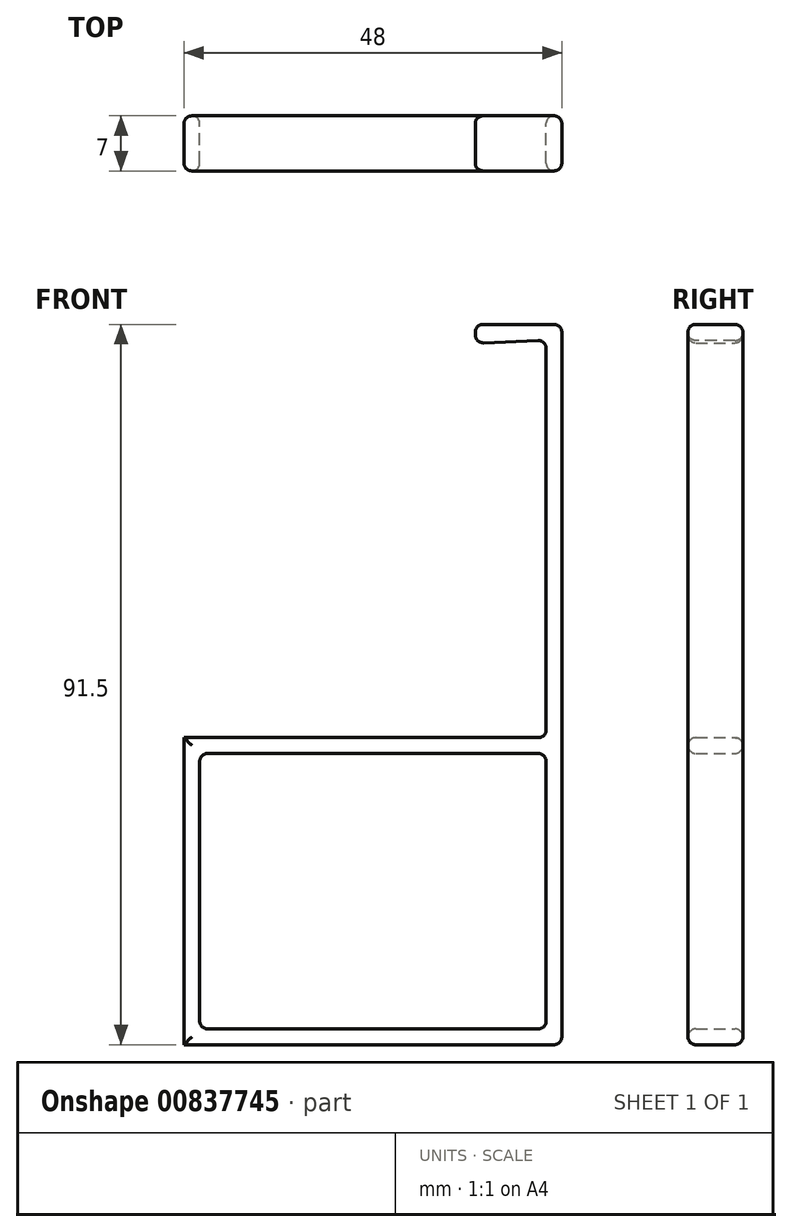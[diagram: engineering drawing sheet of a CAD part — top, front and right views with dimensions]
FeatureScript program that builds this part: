
annotation { "Feature Type Name" : "Feature", "Feature Type Description" : "" }
export const myFeature = defineFeature(function(context is Context, id is Id, definition is map)
    precondition{}
    {
        {
            var Q0;
            Q0=qCreatedBy(makeId("Front.planeOp"),FACE);
            var sketch = newSketch(context, id + "F0", { "sketchPlane" : qUnion([Q0])});
            skLineSegment(sketch, "E0", {"start": v(-54.27, 63.8) * mm, "end": v(-45.27, 64.18) * mm});
            skLineSegment(sketch, "E1", {"start": v(-45.27, 64.18) * mm, "end": v(-45.27, 13.68) * mm});
            skLineSegment(sketch, "E2", {"start": v(-45.27, 13.68) * mm, "end": v(-45.27, 13.68) * mm});
            skLineSegment(sketch, "E3", {"start": v(-45.27, -23.32) * mm, "end": v(-89.27, -23.32) * mm});
            skLineSegment(sketch, "E4", {"start": v(-91.27, -23.32) * mm, "end": v(-91.27, -25.32) * mm});
            skLineSegment(sketch, "E5", {"start": v(-91.27, -25.32) * mm, "end": v(-43.27, -25.32) * mm});
            skLineSegment(sketch, "E6", {"start": v(-43.27, -25.32) * mm, "end": v(-43.27, 66.18) * mm});
            skLineSegment(sketch, "E7", {"start": v(-43.27, 66.18) * mm, "end": v(-54.27, 66.18) * mm});
            skLineSegment(sketch, "E8", {"start": v(-54.27, 66.18) * mm, "end": v(-54.27, 63.8) * mm});
            skLineSegment(sketch, "E9", {"start": v(-45.27, 11.68) * mm, "end": v(-45.27, 11.68) * mm});
            skLineSegment(sketch, "E10", {"start": v(-45.27, 11.68) * mm, "end": v(-45.27, -23.32) * mm});
            skLineSegment(sketch, "E11", {"start": v(-45.27, 13.68) * mm, "end": v(-91.27, 13.68) * mm});
            skLineSegment(sketch, "E12", {"start": v(-91.27, 13.68) * mm, "end": v(-91.27, 11.68) * mm});
            skLineSegment(sketch, "E13", {"start": v(-89.27, 11.68) * mm, "end": v(-45.27, 11.68) * mm});
            skLineSegment(sketch, "E14", {"start": v(-91.27, 11.68) * mm, "end": v(-91.27, -23.32) * mm});
            skLineSegment(sketch, "E15", {"start": v(-89.27, -23.32) * mm, "end": v(-89.27, 11.68) * mm});
            skSolve(sketch);
        }
        {
            var Q0;
            Q0=makeQuery(id+"F0.imprint","IMPRINT",FACE,{"disambiguationData":[TD([[makeQuery(id+"F0.imprint","IMPRINT",EDGE,{"derivedFrom":sQuery(id+"F0.wireOp",EDGE,"E0")}),1.0]])]});
            extrude(context, id + "F1", {"entities" : qUnion([Q0]), "depth" : 7 * mm, "offsetDistance" : 25 * mm});
        }
        {
            var Q0;
            Q0=makeQuery(id+"F1.opExtrude","CAP_FACE",FACE,{"disambiguationData":[OSD([sQuery(id+"F0.wireOp",EDGE,"E0"),sQuery(id+"F0.wireOp",EDGE,"E1"),sQuery(id+"F0.wireOp",EDGE,"E3"),sQuery(id+"F0.wireOp",EDGE,"E4"),sQuery(id+"F0.wireOp",EDGE,"E5"),sQuery(id+"F0.wireOp",EDGE,"E6"),sQuery(id+"F0.wireOp",EDGE,"E7"),sQuery(id+"F0.wireOp",EDGE,"E8"),sQuery(id+"F0.wireOp",EDGE,"E10"),sQuery(id+"F0.wireOp",EDGE,"E11"),sQuery(id+"F0.wireOp",EDGE,"E12"),sQuery(id+"F0.wireOp",EDGE,"E13"),sQuery(id+"F0.wireOp",EDGE,"E14"),sQuery(id+"F0.wireOp",EDGE,"E15")])],"isStart":false});
            var Q1;
            Q1=makeQuery(id+"F1.opExtrude","CAP_FACE",FACE,{"disambiguationData":[OSD([sQuery(id+"F0.wireOp",EDGE,"E0"),sQuery(id+"F0.wireOp",EDGE,"E1"),sQuery(id+"F0.wireOp",EDGE,"E3"),sQuery(id+"F0.wireOp",EDGE,"E4"),sQuery(id+"F0.wireOp",EDGE,"E5"),sQuery(id+"F0.wireOp",EDGE,"E6"),sQuery(id+"F0.wireOp",EDGE,"E7"),sQuery(id+"F0.wireOp",EDGE,"E8"),sQuery(id+"F0.wireOp",EDGE,"E10"),sQuery(id+"F0.wireOp",EDGE,"E11"),sQuery(id+"F0.wireOp",EDGE,"E12"),sQuery(id+"F0.wireOp",EDGE,"E13"),sQuery(id+"F0.wireOp",EDGE,"E14"),sQuery(id+"F0.wireOp",EDGE,"E15")])],"isStart":true});
            var Q2;
            Q2=makeQuery(id+"F1.opExtrude","SWEPT_EDGE",EDGE,{"disambiguationData":[OSD([sQuery(id+"F0.wireOp",EDGE,"E10"),sQuery(id+"F0.wireOp",EDGE,"E13")])]});
            var Q3;
            Q3=makeQuery(id+"F1.opExtrude","SWEPT_EDGE",EDGE,{"disambiguationData":[OSD([sQuery(id+"F0.wireOp",EDGE,"E3"),sQuery(id+"F0.wireOp",EDGE,"E10")])]});
            var Q4;
            Q4=makeQuery(id+"F1.opExtrude","SWEPT_EDGE",EDGE,{"disambiguationData":[OSD([sQuery(id+"F0.wireOp",EDGE,"E13"),sQuery(id+"F0.wireOp",EDGE,"E15")])]});
            var Q5;
            Q5=makeQuery(id+"F1.opExtrude","SWEPT_EDGE",EDGE,{"disambiguationData":[OSD([sQuery(id+"F0.wireOp",EDGE,"E3"),sQuery(id+"F0.wireOp",EDGE,"E15")])]});
            var Q6;
            Q6=makeQuery(id+"F1.opExtrude","SWEPT_EDGE",EDGE,{"disambiguationData":[OSD([sQuery(id+"F0.wireOp",EDGE,"E0"),sQuery(id+"F0.wireOp",EDGE,"E8")])]});
            var Q7;
            Q7=makeQuery(id+"F1.opExtrude","SWEPT_EDGE",EDGE,{"disambiguationData":[OSD([sQuery(id+"F0.wireOp",EDGE,"E0"),sQuery(id+"F0.wireOp",EDGE,"E1")])]});
            var Q8;
            Q8=makeQuery(id+"F1.opExtrude","SWEPT_EDGE",EDGE,{"disambiguationData":[OSD([sQuery(id+"F0.wireOp",EDGE,"E7"),sQuery(id+"F0.wireOp",EDGE,"E8")])]});
            var Q9;
            Q9=makeQuery(id+"F1.opExtrude","SWEPT_EDGE",EDGE,{"disambiguationData":[OSD([sQuery(id+"F0.wireOp",EDGE,"E6"),sQuery(id+"F0.wireOp",EDGE,"E7")])]});
            var Q10;
            Q10=makeQuery(id+"F1.opExtrude","SWEPT_EDGE",EDGE,{"disambiguationData":[OSD([sQuery(id+"F0.wireOp",EDGE,"E1"),sQuery(id+"F0.wireOp",EDGE,"E11")])]});
            var Q11;
            Q11=makeQuery(id+"F1.opExtrude","SWEPT_EDGE",EDGE,{"disambiguationData":[OSD([sQuery(id+"F0.wireOp",EDGE,"E5"),sQuery(id+"F0.wireOp",EDGE,"E6")])]});
            fillet(context, id + "F2", {"entities" : qUnion([Q0, Q1, Q2, Q3, Q4, Q5, Q6, Q7, Q8, Q9, Q10, Q11]), "tangentPropagation" : true, "radius" : 1 * mm, "defaultsChanged" : false, "vertexSettings" : [], "allowEdgeOverflow" : false});
        }
    });
